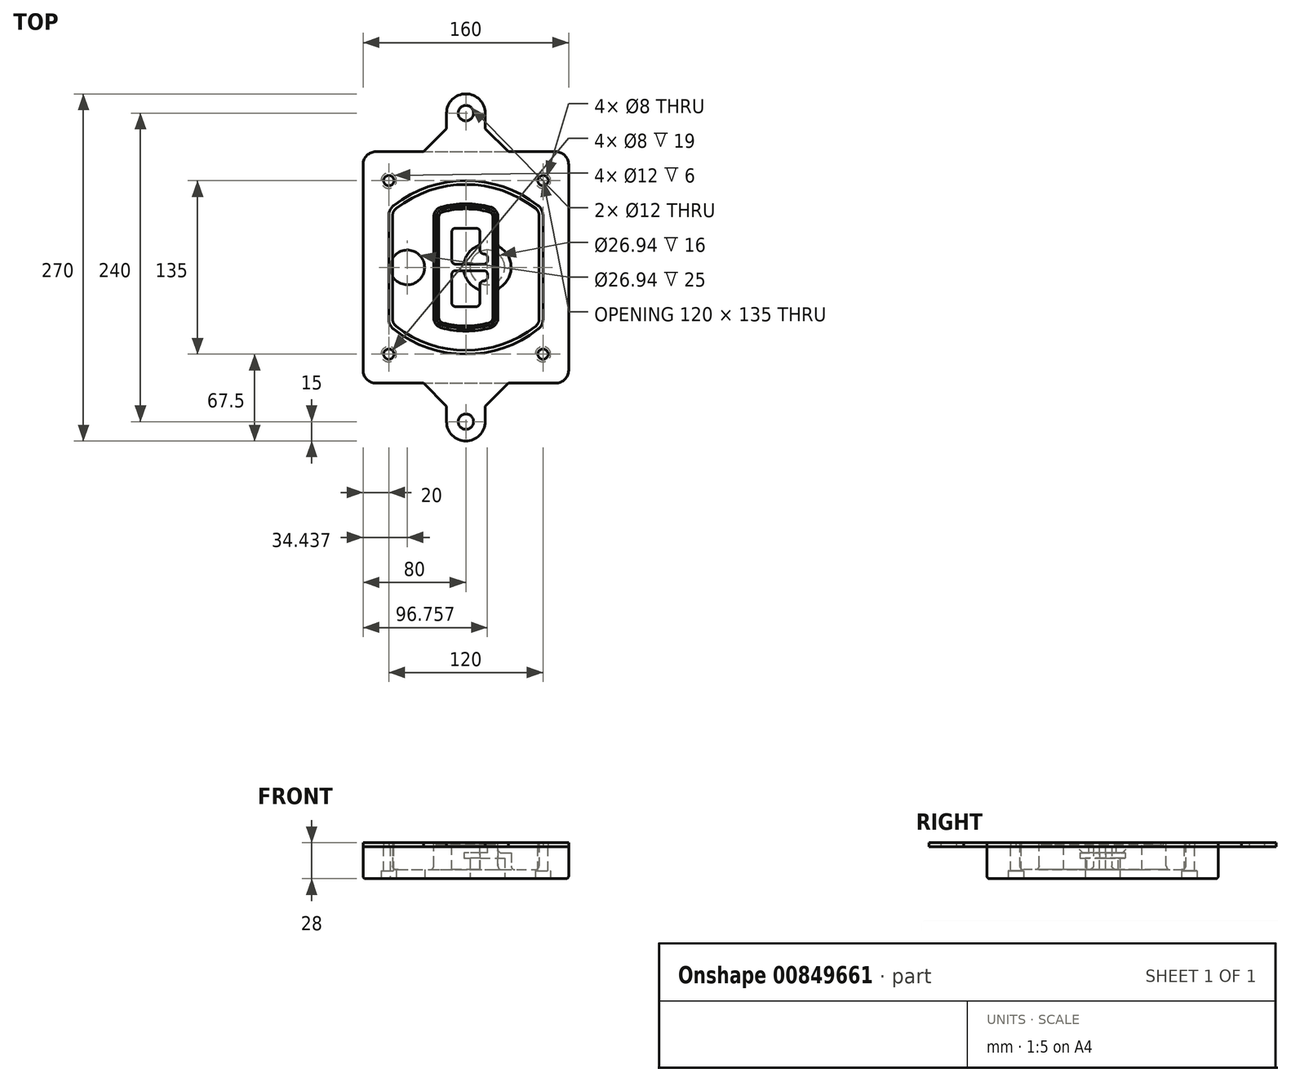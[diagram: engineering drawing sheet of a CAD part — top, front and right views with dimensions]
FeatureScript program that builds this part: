
annotation { "Feature Type Name" : "Feature", "Feature Type Description" : "" }
export const myFeature = defineFeature(function(context is Context, id is Id, definition is map)
    precondition{}
    {
        {
            var Q0;
            Q0=qCreatedBy(makeId("Top.planeOp"),FACE);
            var sketch = newSketch(context, id + "F0", { "sketchPlane" : qUnion([Q0])});
            skPoint(sketch, "E0.rect.middle", {"position": v(0, 0) * mm});
            skLineSegment(sketch, "E1.bottom", {"start": v(-70, -90) * mm, "end": v(70, -90) * mm});
            skLineSegment(sketch, "E1.top", {"start": v(-70, 90) * mm, "end": v(70, 90) * mm});
            skLineSegment(sketch, "E1.left", {"start": v(-80, -80) * mm, "end": v(-80, 80) * mm});
            skLineSegment(sketch, "E1.right", {"start": v(80, -80) * mm, "end": v(80, 80) * mm});
            skLineSegment(sketch, "E2", {"start": v(-80, 90) * mm, "end": v(80, -90) * mm, "construction": true});
            skLineSegment(sketch, "E3", {"start": v(80, 90) * mm, "end": v(-80, -90) * mm, "construction": true});
            skCircle(sketch, "E4", {"center": v(-60, 67.5) * mm, "radius": 4 * mm});
            skCircle(sketch, "E5", {"center": v(60, 67.5) * mm, "radius": 4 * mm});
            skCircle(sketch, "E6", {"center": v(60, -67.5) * mm, "radius": 4 * mm});
            skCircle(sketch, "E7", {"center": v(-60, -67.5) * mm, "radius": 4 * mm});
            skLineSegment(sketch, "E8", {"start": v(-60, 67.5) * mm, "end": v(60, 67.5) * mm, "construction": true});
            skLineSegment(sketch, "E9", {"start": v(60, 67.5) * mm, "end": v(60, -67.5) * mm, "construction": true});
            skLineSegment(sketch, "E10", {"start": v(60, -67.5) * mm, "end": v(-60, -67.5) * mm, "construction": true});
            skLineSegment(sketch, "E11", {"start": v(-60, -67.5) * mm, "end": v(-60, 67.5) * mm, "construction": true});
            skLineSegment(sketch, "E12", {"start": v(-60, 40.3) * mm, "end": v(-60, -40.3) * mm});
            skLineSegment(sketch, "E13", {"start": v(60, 40.3) * mm, "end": v(60, -40.3) * mm});
            skArc(sketch, "E14", {"start": v(56.15, 48.18) * mm, "mid": v(0, 67.5) * mm, "end": v(-56.15, 48.18) * mm});
            skArc(sketch, "E15", {"start": v(-56.15, -48.18) * mm, "mid": v(0, -67.5) * mm, "end": v(56.15, -48.18) * mm});
            skLineSegment(sketch, "E16", {"start": v(-60, 0) * mm, "end": v(60, 0) * mm, "construction": true});
            skPoint(sketch, "E17.visualSharp", {"position": v(-60, -45) * mm});
            skArc(sketch, "E17.filletArc", {"start": v(-60, -40.3) * mm, "mid": v(-58.99, -44.68) * mm, "end": v(-56.15, -48.18) * mm});
            skPoint(sketch, "E18.visualSharp", {"position": v(-60, 45) * mm});
            skArc(sketch, "E18.filletArc", {"start": v(-56.15, 48.18) * mm, "mid": v(-58.99, 44.68) * mm, "end": v(-60, 40.3) * mm});
            skPoint(sketch, "E19.visualSharp", {"position": v(60, 45) * mm});
            skArc(sketch, "E19.filletArc", {"start": v(60, 40.3) * mm, "mid": v(58.99, 44.68) * mm, "end": v(56.15, 48.18) * mm});
            skPoint(sketch, "E20.visualSharp", {"position": v(60, -45) * mm});
            skArc(sketch, "E20.filletArc", {"start": v(56.15, -48.18) * mm, "mid": v(58.99, -44.68) * mm, "end": v(60, -40.3) * mm});
            skPoint(sketch, "E21.visualSharp", {"position": v(-80, 90) * mm});
            skArc(sketch, "E21.filletArc", {"start": v(-70, 90) * mm, "mid": v(-77.07, 87.07) * mm, "end": v(-80, 80) * mm});
            skPoint(sketch, "E22.visualSharp", {"position": v(80, 90) * mm});
            skArc(sketch, "E22.filletArc", {"start": v(80, 80) * mm, "mid": v(77.07, 87.07) * mm, "end": v(70, 90) * mm});
            skPoint(sketch, "E23.visualSharp", {"position": v(80, -90) * mm});
            skArc(sketch, "E23.filletArc", {"start": v(70, -90) * mm, "mid": v(77.07, -87.07) * mm, "end": v(80, -80) * mm});
            skPoint(sketch, "E24.visualSharp", {"position": v(-80, -90) * mm});
            skArc(sketch, "E24.filletArc", {"start": v(-80, -80) * mm, "mid": v(-77.07, -87.07) * mm, "end": v(-70, -90) * mm});
            skArc(sketch, "E25.0", {"start": v(57, 40.3) * mm, "mid": v(56.3, 43.36) * mm, "end": v(54.3, 45.81) * mm});
            skLineSegment(sketch, "E25.1", {"start": v(57, 40.3) * mm, "end": v(57, -40.3) * mm});
            skArc(sketch, "E25.2", {"start": v(54.3, -45.81) * mm, "mid": v(56.3, -43.36) * mm, "end": v(57, -40.3) * mm});
            skArc(sketch, "E25.3", {"start": v(-54.3, -45.81) * mm, "mid": v(0, -64.5) * mm, "end": v(54.3, -45.81) * mm});
            skArc(sketch, "E25.4", {"start": v(-57, -40.3) * mm, "mid": v(-56.3, -43.36) * mm, "end": v(-54.3, -45.81) * mm});
            skArc(sketch, "E25.5", {"start": v(54.3, 45.81) * mm, "mid": v(0, 64.5) * mm, "end": v(-54.3, 45.81) * mm});
            skLineSegment(sketch, "E25.6", {"start": v(-57, 40.3) * mm, "end": v(-57, -40.3) * mm});
            skArc(sketch, "E25.7", {"start": v(-54.3, 45.81) * mm, "mid": v(-56.3, 43.36) * mm, "end": v(-57, 40.3) * mm});
            skArc(sketch, "E26.0", {"start": v(-58.62, 51.33) * mm, "mid": v(-62.58, 46.43) * mm, "end": v(-64, 40.3) * mm});
            skArc(sketch, "E26.1", {"start": v(58.62, 51.33) * mm, "mid": v(0, 71.5) * mm, "end": v(-58.62, 51.33) * mm});
            skArc(sketch, "E26.2", {"start": v(64, 40.3) * mm, "mid": v(62.58, 46.43) * mm, "end": v(58.62, 51.33) * mm});
            skLineSegment(sketch, "E26.3", {"start": v(64, 40.3) * mm, "end": v(64, -40.3) * mm});
            skArc(sketch, "E26.4", {"start": v(58.62, -51.33) * mm, "mid": v(62.58, -46.43) * mm, "end": v(64, -40.3) * mm});
            skLineSegment(sketch, "E26.5", {"start": v(-64, 40.3) * mm, "end": v(-64, -40.3) * mm});
            skArc(sketch, "E26.6", {"start": v(-58.62, -51.33) * mm, "mid": v(0, -71.5) * mm, "end": v(58.62, -51.33) * mm});
            skArc(sketch, "E26.7", {"start": v(-64, -40.3) * mm, "mid": v(-62.58, -46.43) * mm, "end": v(-58.62, -51.33) * mm});
            skSolve(sketch);
        }
        {
            var Q0;
            Q0=makeQuery(id+"F0.imprint","IMPRINT",FACE,{"disambiguationData":[TD([[makeQuery(id+"F0.imprint","IMPRINT",EDGE,{"derivedFrom":sQuery(id+"F0.wireOp",EDGE,"E1.bottom")}),1.0]])]});
            var Q1;
            Q1=makeQuery(id+"F0.imprint","IMPRINT",FACE,{"disambiguationData":[TD([[makeQuery(id+"F0.imprint","IMPRINT",EDGE,{"derivedFrom":sQuery(id+"F0.wireOp",EDGE,"E12")}),1.0]])]});
            var Q2;
            Q2=makeQuery(id+"F0.imprint","IMPRINT",FACE,{"disambiguationData":[TD([[makeQuery(id+"F0.imprint","IMPRINT",EDGE,{"derivedFrom":sQuery(id+"F0.wireOp",EDGE,"E25.0")}),1.0]])]});
            var Q3;
            Q3=makeQuery(id+"F0.imprint","IMPRINT",FACE,{"disambiguationData":[TD([[makeQuery(id+"F0.imprint","IMPRINT",EDGE,{"derivedFrom":sQuery(id+"F0.wireOp",EDGE,"E12")}),-1.0]])]});
            extrude(context, id + "F1", {"entities" : qUnion([Q0, Q1, Q2, Q3]), "oppositeDirection" : true, "depth" : 25 * mm});
        }
        {
            var Q0;
            Q0=makeQuery(id+"F0.imprint","IMPRINT",FACE,{"disambiguationData":[TD([[makeQuery(id+"F0.imprint","IMPRINT",EDGE,{"derivedFrom":sQuery(id+"F0.wireOp",EDGE,"E12")}),1.0]])]});
            extrude(context, id + "F2", {"entities" : qUnion([Q0]), "operationType" : NewBodyOperationType.ADD, "depth" : 3 * mm});
        }
        {
            var Q0;
            Q0=makeQuery(id+"F0.imprint","IMPRINT",FACE,{"disambiguationData":[TD([[makeQuery(id+"F0.imprint","IMPRINT",EDGE,{"derivedFrom":sQuery(id+"F0.wireOp",EDGE,"E25.0")}),1.0]])]});
            extrude(context, id + "F3", {"entities" : qUnion([Q0]), "operationType" : NewBodyOperationType.REMOVE, "oppositeDirection" : true, "depth" : 18 * mm});
        }
        {
            var Q0;
            Q0=makeQuery(id+"F2.opExtrude","CAP_FACE",FACE,{"disambiguationData":[OSD([sQuery(id+"F0.wireOp",EDGE,"E12"),sQuery(id+"F0.wireOp",EDGE,"E13"),sQuery(id+"F0.wireOp",EDGE,"E14"),sQuery(id+"F0.wireOp",EDGE,"E15"),sQuery(id+"F0.wireOp",EDGE,"E17.filletArc"),sQuery(id+"F0.wireOp",EDGE,"E18.filletArc"),sQuery(id+"F0.wireOp",EDGE,"E19.filletArc"),sQuery(id+"F0.wireOp",EDGE,"E20.filletArc"),sQuery(id+"F0.wireOp",EDGE,"E25.0"),sQuery(id+"F0.wireOp",EDGE,"E25.1"),sQuery(id+"F0.wireOp",EDGE,"E25.2"),sQuery(id+"F0.wireOp",EDGE,"E25.3"),sQuery(id+"F0.wireOp",EDGE,"E25.4"),sQuery(id+"F0.wireOp",EDGE,"E25.5"),sQuery(id+"F0.wireOp",EDGE,"E25.6"),sQuery(id+"F0.wireOp",EDGE,"E25.7")])],"isStart":false});
            var sketch = newSketch(context, id + "F4", { "sketchPlane" : qUnion([Q0])});
            skArc(sketch, "E27.0", {"start": v(-19.08, -46.97) * mm, "mid": v(0, -49.5) * mm, "end": v(19.08, -46.97) * mm});
            skArc(sketch, "E28.0", {"start": v(19.08, 46.97) * mm, "mid": v(0, 49.5) * mm, "end": v(-19.08, 46.97) * mm});
            skLineSegment(sketch, "E29", {"start": v(-25, 39.25) * mm, "end": v(-25, -39.25) * mm});
            skLineSegment(sketch, "E30", {"start": v(25, 39.25) * mm, "end": v(25, -39.25) * mm});
            skLineSegment(sketch, "E31", {"start": v(-25, 45.1) * mm, "end": v(25, 45.1) * mm, "construction": true});
            skLineSegment(sketch, "E32", {"start": v(-25, -45.1) * mm, "end": v(25, -45.1) * mm, "construction": true});
            skPoint(sketch, "E33.visualSharp", {"position": v(-25, 45.1) * mm});
            skArc(sketch, "E33.filletArc", {"start": v(-19.08, 46.97) * mm, "mid": v(-23.35, 44.11) * mm, "end": v(-25, 39.25) * mm});
            skPoint(sketch, "E34.visualSharp", {"position": v(25, 45.1) * mm});
            skArc(sketch, "E34.filletArc", {"start": v(25, 39.25) * mm, "mid": v(23.35, 44.11) * mm, "end": v(19.08, 46.97) * mm});
            skPoint(sketch, "E35.visualSharp", {"position": v(25, -45.1) * mm});
            skArc(sketch, "E35.filletArc", {"start": v(19.08, -46.97) * mm, "mid": v(23.35, -44.11) * mm, "end": v(25, -39.25) * mm});
            skPoint(sketch, "E36.visualSharp", {"position": v(-25, -45.1) * mm});
            skArc(sketch, "E36.filletArc", {"start": v(-25, -39.25) * mm, "mid": v(-23.35, -44.11) * mm, "end": v(-19.08, -46.97) * mm});
            skArc(sketch, "E37.0", {"start": v(54.3, 45.81) * mm, "mid": v(0, 64.5) * mm, "end": v(-54.3, 45.81) * mm});
            skArc(sketch, "E37.1", {"start": v(-54.3, 45.81) * mm, "mid": v(-56.3, 43.36) * mm, "end": v(-57, 40.3) * mm});
            skLineSegment(sketch, "E37.2", {"start": v(-57, 40.3) * mm, "end": v(-57, -40.3) * mm});
            skArc(sketch, "E37.3", {"start": v(-57, -40.3) * mm, "mid": v(-56.3, -43.36) * mm, "end": v(-54.3, -45.81) * mm});
            skArc(sketch, "E37.4", {"start": v(-54.3, -45.81) * mm, "mid": v(0, -64.5) * mm, "end": v(54.3, -45.81) * mm});
            skArc(sketch, "E37.5", {"start": v(54.3, -45.81) * mm, "mid": v(56.3, -43.36) * mm, "end": v(57, -40.3) * mm});
            skLineSegment(sketch, "E37.6", {"start": v(57, 40.3) * mm, "end": v(57, -40.3) * mm});
            skArc(sketch, "E37.7", {"start": v(57, 40.3) * mm, "mid": v(56.3, 43.36) * mm, "end": v(54.3, 45.81) * mm});
            skLineSegment(sketch, "E38.0", {"start": v(23, 39.25) * mm, "end": v(23, -39.25) * mm});
            skArc(sketch, "E38.1", {"start": v(18.56, -45.04) * mm, "mid": v(21.76, -42.9) * mm, "end": v(23, -39.25) * mm});
            skArc(sketch, "E38.2", {"start": v(-18.56, -45.04) * mm, "mid": v(0, -47.5) * mm, "end": v(18.56, -45.04) * mm});
            skArc(sketch, "E38.3", {"start": v(-23, -39.25) * mm, "mid": v(-21.76, -42.9) * mm, "end": v(-18.56, -45.04) * mm});
            skLineSegment(sketch, "E38.4", {"start": v(-23, 39.25) * mm, "end": v(-23, -39.25) * mm});
            skArc(sketch, "E38.5", {"start": v(23, 39.25) * mm, "mid": v(21.76, 42.9) * mm, "end": v(18.56, 45.04) * mm});
            skArc(sketch, "E38.6", {"start": v(-18.56, 45.04) * mm, "mid": v(-21.76, 42.9) * mm, "end": v(-23, 39.25) * mm});
            skArc(sketch, "E38.7", {"start": v(18.56, 45.04) * mm, "mid": v(0, 47.5) * mm, "end": v(-18.56, 45.04) * mm});
            skArc(sketch, "E39.0", {"start": v(21, 39.25) * mm, "mid": v(20.18, 41.68) * mm, "end": v(18.04, 43.1) * mm});
            skLineSegment(sketch, "E39.1", {"start": v(21, 39.25) * mm, "end": v(21, -39.25) * mm});
            skArc(sketch, "E39.2", {"start": v(18.04, -43.1) * mm, "mid": v(20.18, -41.68) * mm, "end": v(21, -39.25) * mm});
            skArc(sketch, "E39.3", {"start": v(-18.04, -43.1) * mm, "mid": v(0, -45.5) * mm, "end": v(18.04, -43.1) * mm});
            skArc(sketch, "E39.4", {"start": v(-21, -39.25) * mm, "mid": v(-20.18, -41.68) * mm, "end": v(-18.04, -43.1) * mm});
            skArc(sketch, "E39.5", {"start": v(18.04, 43.1) * mm, "mid": v(0, 45.5) * mm, "end": v(-18.04, 43.1) * mm});
            skLineSegment(sketch, "E39.6", {"start": v(-21, 39.25) * mm, "end": v(-21, -39.25) * mm});
            skArc(sketch, "E39.7", {"start": v(-18.04, 43.1) * mm, "mid": v(-20.18, 41.68) * mm, "end": v(-21, 39.25) * mm});
            skLineSegment(sketch, "E40", {"start": v(-25, 0) * mm, "end": v(25, 0) * mm, "construction": true});
            skLineSegment(sketch, "E41", {"start": v(-11, 5.5) * mm, "end": v(-11, 27.5) * mm});
            skLineSegment(sketch, "E42", {"start": v(-8, 30.5) * mm, "end": v(8, 30.5) * mm});
            skLineSegment(sketch, "E43", {"start": v(11, 27.5) * mm, "end": v(11, 13.5) * mm});
            skLineSegment(sketch, "E44", {"start": v(14, 10.5) * mm, "end": v(14, 10.5) * mm});
            skLineSegment(sketch, "E45", {"start": v(17, 7.5) * mm, "end": v(17, 5.5) * mm});
            skLineSegment(sketch, "E46", {"start": v(14, 2.5) * mm, "end": v(-8, 2.5) * mm});
            skPoint(sketch, "E47.visualSharp", {"position": v(-11, 30.5) * mm});
            skArc(sketch, "E47.filletArc", {"start": v(-8, 30.5) * mm, "mid": v(-10.12, 29.62) * mm, "end": v(-11, 27.5) * mm});
            skPoint(sketch, "E48.visualSharp", {"position": v(11, 30.5) * mm});
            skArc(sketch, "E48.filletArc", {"start": v(11, 27.5) * mm, "mid": v(10.12, 29.62) * mm, "end": v(8, 30.5) * mm});
            skPoint(sketch, "E49.visualSharp", {"position": v(11, 10.5) * mm});
            skArc(sketch, "E49.filletArc", {"start": v(11, 13.5) * mm, "mid": v(11.88, 11.38) * mm, "end": v(14, 10.5) * mm});
            skPoint(sketch, "E50.visualSharp", {"position": v(17, 10.5) * mm});
            skArc(sketch, "E50.filletArc", {"start": v(17, 7.5) * mm, "mid": v(16.12, 9.62) * mm, "end": v(14, 10.5) * mm});
            skPoint(sketch, "E51.visualSharp", {"position": v(17, 2.5) * mm});
            skArc(sketch, "E51.filletArc", {"start": v(14, 2.5) * mm, "mid": v(16.12, 3.38) * mm, "end": v(17, 5.5) * mm});
            skPoint(sketch, "E52.visualSharp", {"position": v(-11, 2.5) * mm});
            skArc(sketch, "E52.filletArc", {"start": v(-11, 5.5) * mm, "mid": v(-10.12, 3.38) * mm, "end": v(-8, 2.5) * mm});
            skLineSegment(sketch, "E53.0.MirrorCS", {"start": v(14, -2.5) * mm, "end": v(-8, -2.5) * mm});
            skArc(sketch, "E54.0.MirrorCS", {"start": v(-11, -5.5) * mm, "mid": v(-10.12, -3.38) * mm, "end": v(-8, -2.5) * mm});
            skLineSegment(sketch, "E55.0.MirrorCS", {"start": v(-11, -5.5) * mm, "end": v(-11, -27.5) * mm});
            skArc(sketch, "E56.0.MirrorCS", {"start": v(-8, -30.5) * mm, "mid": v(-10.12, -29.62) * mm, "end": v(-11, -27.5) * mm});
            skLineSegment(sketch, "E57.0.MirrorCS", {"start": v(-8, -30.5) * mm, "end": v(8, -30.5) * mm});
            skArc(sketch, "E58.0.MirrorCS", {"start": v(11, -27.5) * mm, "mid": v(10.12, -29.62) * mm, "end": v(8, -30.5) * mm});
            skLineSegment(sketch, "E59.0.MirrorCS", {"start": v(11, -27.5) * mm, "end": v(11, -13.5) * mm});
            skArc(sketch, "E60.0.MirrorCS", {"start": v(11, -13.5) * mm, "mid": v(11.88, -11.38) * mm, "end": v(14, -10.5) * mm});
            skArc(sketch, "E61.0.MirrorCS", {"start": v(17, -7.5) * mm, "mid": v(16.12, -9.62) * mm, "end": v(14, -10.5) * mm});
            skLineSegment(sketch, "E62.0.MirrorCS", {"start": v(17, -7.5) * mm, "end": v(17, -5.5) * mm});
            skArc(sketch, "E63.0.MirrorCS", {"start": v(14, -2.5) * mm, "mid": v(16.12, -3.38) * mm, "end": v(17, -5.5) * mm});
            skSolve(sketch);
        }
        {
            var Q0;
            Q0=makeQuery(id+"F4.imprint","IMPRINT",FACE,{"disambiguationData":[TD([[makeQuery(id+"F4.imprint","IMPRINT",EDGE,{"derivedFrom":sQuery(id+"F4.wireOp",EDGE,"E27.0")}),1.0]])]});
            var Q1;
            Q1=makeQuery(id+"F4.imprint","IMPRINT",FACE,{"disambiguationData":[TD([[makeQuery(id+"F4.imprint","IMPRINT",EDGE,{"derivedFrom":sQuery(id+"F4.wireOp",EDGE,"E38.0")}),-1.0]])]});
            var Q2;
            Q2=makeQuery(id+"F4.imprint","IMPRINT",FACE,{"disambiguationData":[TD([[makeQuery(id+"F4.imprint","IMPRINT",EDGE,{"derivedFrom":sQuery(id+"F4.wireOp",EDGE,"E39.0")}),1.0]])]});
            extrude(context, id + "F5", {"entities" : qUnion([Q0, Q1, Q2]), "operationType" : NewBodyOperationType.ADD, "endBound" : BoundingType.UP_TO_NEXT, "oppositeDirection" : true, "depth" : 25 * mm});
        }
        {
            var Q0;
            Q0=makeQuery(id+"F4.imprint","IMPRINT",FACE,{"disambiguationData":[TD([[makeQuery(id+"F4.imprint","IMPRINT",EDGE,{"derivedFrom":sQuery(id+"F4.wireOp",EDGE,"E38.0")}),-1.0]])]});
            extrude(context, id + "F6", {"entities" : qUnion([Q0]), "operationType" : NewBodyOperationType.REMOVE, "oppositeDirection" : true, "depth" : 2 * mm});
        }
        {
            var Q0;
            Q0=makeQuery(id+"F1.opExtrude","CAP_FACE",FACE,{"disambiguationData":[OSD([sQuery(id+"F0.wireOp",EDGE,"E1.bottom"),sQuery(id+"F0.wireOp",EDGE,"E1.top"),sQuery(id+"F0.wireOp",EDGE,"E1.left"),sQuery(id+"F0.wireOp",EDGE,"E1.right"),sQuery(id+"F0.wireOp",EDGE,"E4"),sQuery(id+"F0.wireOp",EDGE,"E5"),sQuery(id+"F0.wireOp",EDGE,"E6"),sQuery(id+"F0.wireOp",EDGE,"E7"),sQuery(id+"F0.wireOp",EDGE,"E21.filletArc"),sQuery(id+"F0.wireOp",EDGE,"E22.filletArc"),sQuery(id+"F0.wireOp",EDGE,"E23.filletArc"),sQuery(id+"F0.wireOp",EDGE,"E24.filletArc")])],"isStart":false});
            var sketch = newSketch(context, id + "F7", { "sketchPlane" : qUnion([Q0])});
            skCircle(sketch, "E64", {"center": v(16.76, 0) * mm, "radius": 13.47 * mm});
            skCircle(sketch, "E65", {"center": v(-45.56, 0) * mm, "radius": 13.47 * mm});
            skLineSegment(sketch, "E66", {"start": v(80, 0) * mm, "end": v(-80, 0) * mm});
            skCircle(sketch, "E67", {"center": v(16.76, 0) * mm, "radius": 18.47 * mm});
            skCircle(sketch, "E68", {"center": v(60, -67.5) * mm, "radius": 6 * mm});
            skCircle(sketch, "E69", {"center": v(-60, -67.5) * mm, "radius": 6 * mm});
            skCircle(sketch, "E70", {"center": v(-60, 67.5) * mm, "radius": 6 * mm});
            skCircle(sketch, "E71", {"center": v(60, 67.5) * mm, "radius": 6 * mm});
            skSolve(sketch);
        }
        {
            var Q0;
            {var subQ1=sQuery(id+"F7.wireOp",EDGE,"E66");var subQ4=sQuery(id+"F7.wireOp",EDGE,"E64");var subQ6=makeQuery(id+"F7.imprint","INTERSECT",VERTEX,{"disambiguationData":[OD(0.0)],"derivedFrom":[subQ4,subQ1]});Q0=makeQuery(id+"F7.imprint","IMPRINT",FACE,{"disambiguationData":[TD([[makeQuery(id+"F7.imprint","IMPRINT",EDGE,{"disambiguationData":[TD([[subQ6,-1.0]])],"derivedFrom":subQ4}),-1.0]])]});}
            var Q1;
            {var subQ0=sQuery(id+"F7.wireOp",EDGE,"E66");var subQ1=sQuery(id+"F7.wireOp",EDGE,"E64");var subQ3=makeQuery(id+"F7.imprint","INTERSECT",VERTEX,{"disambiguationData":[OD(0.0)],"derivedFrom":[subQ1,subQ0]});Q1=makeQuery(id+"F7.imprint","IMPRINT",FACE,{"disambiguationData":[TD([[makeQuery(id+"F7.imprint","IMPRINT",EDGE,{"disambiguationData":[TD([[subQ3,-1.0]])],"derivedFrom":subQ1}),1.0]])]});}
            var Q2;
            {var subQ0=sQuery(id+"F7.wireOp",EDGE,"E66");var subQ1=sQuery(id+"F7.wireOp",EDGE,"E64");var subQ3=makeQuery(id+"F7.imprint","INTERSECT",VERTEX,{"disambiguationData":[OD(0.0)],"derivedFrom":[subQ1,subQ0]});Q2=makeQuery(id+"F7.imprint","IMPRINT",FACE,{"disambiguationData":[TD([[makeQuery(id+"F7.imprint","IMPRINT",EDGE,{"disambiguationData":[TD([[subQ3,1.0]])],"derivedFrom":subQ1}),1.0]])]});}
            var Q3;
            {var subQ1=sQuery(id+"F7.wireOp",EDGE,"E66");var subQ4=sQuery(id+"F7.wireOp",EDGE,"E64");var subQ6=makeQuery(id+"F7.imprint","INTERSECT",VERTEX,{"disambiguationData":[OD(0.0)],"derivedFrom":[subQ4,subQ1]});Q3=makeQuery(id+"F7.imprint","IMPRINT",FACE,{"disambiguationData":[TD([[makeQuery(id+"F7.imprint","IMPRINT",EDGE,{"disambiguationData":[TD([[subQ6,1.0]])],"derivedFrom":subQ4}),-1.0]])]});}
            extrude(context, id + "F8", {"entities" : qUnion([Q0, Q1, Q2, Q3]), "operationType" : NewBodyOperationType.ADD, "oppositeDirection" : true, "depth" : 20 * mm});
        }
        {
            var Q0;
            {var subQ0=sQuery(id+"F7.wireOp",EDGE,"E66");var subQ1=sQuery(id+"F7.wireOp",EDGE,"E64");var subQ3=makeQuery(id+"F7.imprint","INTERSECT",VERTEX,{"disambiguationData":[OD(0.0)],"derivedFrom":[subQ1,subQ0]});Q0=makeQuery(id+"F7.imprint","IMPRINT",FACE,{"disambiguationData":[TD([[makeQuery(id+"F7.imprint","IMPRINT",EDGE,{"disambiguationData":[TD([[subQ3,-1.0]])],"derivedFrom":subQ1}),1.0]])]});}
            var Q1;
            {var subQ0=sQuery(id+"F7.wireOp",EDGE,"E66");var subQ1=sQuery(id+"F7.wireOp",EDGE,"E64");var subQ3=makeQuery(id+"F7.imprint","INTERSECT",VERTEX,{"disambiguationData":[OD(0.0)],"derivedFrom":[subQ1,subQ0]});Q1=makeQuery(id+"F7.imprint","IMPRINT",FACE,{"disambiguationData":[TD([[makeQuery(id+"F7.imprint","IMPRINT",EDGE,{"disambiguationData":[TD([[subQ3,1.0]])],"derivedFrom":subQ1}),1.0]])]});}
            extrude(context, id + "F9", {"entities" : qUnion([Q0, Q1]), "operationType" : NewBodyOperationType.REMOVE, "oppositeDirection" : true, "depth" : 16 * mm});
        }
        {
            var Q0;
            {var subQ0=sQuery(id+"F7.wireOp",EDGE,"E66");var subQ1=sQuery(id+"F7.wireOp",EDGE,"E65");var subQ3=makeQuery(id+"F7.imprint","INTERSECT",VERTEX,{"disambiguationData":[OD(0.0)],"derivedFrom":[subQ1,subQ0]});Q0=makeQuery(id+"F7.imprint","IMPRINT",FACE,{"disambiguationData":[TD([[makeQuery(id+"F7.imprint","IMPRINT",EDGE,{"disambiguationData":[TD([[subQ3,-1.0]])],"derivedFrom":subQ1}),1.0]])]});}
            var Q1;
            {var subQ0=sQuery(id+"F7.wireOp",EDGE,"E66");var subQ1=sQuery(id+"F7.wireOp",EDGE,"E65");var subQ3=makeQuery(id+"F7.imprint","INTERSECT",VERTEX,{"disambiguationData":[OD(0.0)],"derivedFrom":[subQ1,subQ0]});Q1=makeQuery(id+"F7.imprint","IMPRINT",FACE,{"disambiguationData":[TD([[makeQuery(id+"F7.imprint","IMPRINT",EDGE,{"disambiguationData":[TD([[subQ3,1.0]])],"derivedFrom":subQ1}),1.0]])]});}
            extrude(context, id + "F10", {"entities" : qUnion([Q0, Q1]), "operationType" : NewBodyOperationType.REMOVE, "oppositeDirection" : true, "depth" : 25 * mm});
        }
        {
            var Q0;
            Q0=makeQuery(id+"F7.imprint","IMPRINT",FACE,{"disambiguationData":[TD([[makeQuery(id+"F7.imprint","IMPRINT",EDGE,{"derivedFrom":sQuery(id+"F7.wireOp",EDGE,"E68")}),1.0]])]});
            var Q1;
            Q1=makeQuery(id+"F7.imprint","IMPRINT",FACE,{"disambiguationData":[TD([[makeQuery(id+"F7.imprint","IMPRINT",EDGE,{"derivedFrom":makeQuery(id+"F1.opExtrude","CAP_EDGE",EDGE,{"disambiguationData":[OSD([sQuery(id+"F0.wireOp",EDGE,"E5")])],"isStart":false})}),-1.0]])]});
            var Q2;
            Q2=makeQuery(id+"F7.imprint","IMPRINT",FACE,{"disambiguationData":[TD([[makeQuery(id+"F7.imprint","IMPRINT",EDGE,{"derivedFrom":sQuery(id+"F7.wireOp",EDGE,"E69")}),1.0]])]});
            var Q3;
            Q3=makeQuery(id+"F7.imprint","IMPRINT",FACE,{"disambiguationData":[TD([[makeQuery(id+"F7.imprint","IMPRINT",EDGE,{"derivedFrom":makeQuery(id+"F1.opExtrude","CAP_EDGE",EDGE,{"disambiguationData":[OSD([sQuery(id+"F0.wireOp",EDGE,"E4")])],"isStart":false})}),-1.0]])]});
            var Q4;
            Q4=makeQuery(id+"F7.imprint","IMPRINT",FACE,{"disambiguationData":[TD([[makeQuery(id+"F7.imprint","IMPRINT",EDGE,{"derivedFrom":sQuery(id+"F7.wireOp",EDGE,"E70")}),1.0]])]});
            var Q5;
            Q5=makeQuery(id+"F7.imprint","IMPRINT",FACE,{"disambiguationData":[TD([[makeQuery(id+"F7.imprint","IMPRINT",EDGE,{"derivedFrom":makeQuery(id+"F1.opExtrude","CAP_EDGE",EDGE,{"disambiguationData":[OSD([sQuery(id+"F0.wireOp",EDGE,"E7")])],"isStart":false})}),-1.0]])]});
            var Q6;
            Q6=makeQuery(id+"F7.imprint","IMPRINT",FACE,{"disambiguationData":[TD([[makeQuery(id+"F7.imprint","IMPRINT",EDGE,{"derivedFrom":sQuery(id+"F7.wireOp",EDGE,"E71")}),1.0]])]});
            var Q7;
            Q7=makeQuery(id+"F7.imprint","IMPRINT",FACE,{"disambiguationData":[TD([[makeQuery(id+"F7.imprint","IMPRINT",EDGE,{"derivedFrom":makeQuery(id+"F1.opExtrude","CAP_EDGE",EDGE,{"disambiguationData":[OSD([sQuery(id+"F0.wireOp",EDGE,"E6")])],"isStart":false})}),-1.0]])]});
            extrude(context, id + "F11", {"entities" : qUnion([Q0, Q1, Q2, Q3, Q4, Q5, Q6, Q7]), "operationType" : NewBodyOperationType.REMOVE, "oppositeDirection" : true, "depth" : 6 * mm});
        }
        {
            var Q0;
            Q0=makeQuery(id+"F9.boolean.opBoolean","COPY",FACE,{"derivedFrom":makeQuery(id+"F9.opExtrude","CAP_FACE",FACE,{"disambiguationData":[OSD([sQuery(id+"F7.wireOp",EDGE,"E64")])],"isStart":false})});
            var sketch = newSketch(context, id + "F12", { "sketchPlane" : qUnion([Q0])});
            skArc(sketch, "E72.0", {"start": v(11, 17.55) * mm, "mid": v(2.57, 11.82) * mm, "end": v(-1.54, 2.5) * mm});
            skArc(sketch, "E72.1", {"start": v(-1.54, -2.5) * mm, "mid": v(2.57, -11.82) * mm, "end": v(11, -17.55) * mm});
            skLineSegment(sketch, "E73", {"start": v(-1.54, -2.5) * mm, "end": v(14, -2.5) * mm});
            skLineSegment(sketch, "E74.0", {"start": v(14, 2.5) * mm, "end": v(-1.54, 2.5) * mm});
            skArc(sketch, "E74.1", {"start": v(14, 2.5) * mm, "mid": v(16.12, 3.38) * mm, "end": v(17, 5.5) * mm});
            skLineSegment(sketch, "E74.2", {"start": v(17, 7.5) * mm, "end": v(17, 5.5) * mm});
            skArc(sketch, "E74.3", {"start": v(17, 7.5) * mm, "mid": v(16.12, 9.62) * mm, "end": v(14, 10.5) * mm});
            skArc(sketch, "E74.4", {"start": v(11, 13.5) * mm, "mid": v(11.88, 11.38) * mm, "end": v(14, 10.5) * mm});
            skLineSegment(sketch, "E74.5", {"start": v(11, 17.55) * mm, "end": v(11, 13.5) * mm});
            skLineSegment(sketch, "E74.7", {"start": v(14, -2.5) * mm, "end": v(-1.54, -2.5) * mm});
            skArc(sketch, "E74.8", {"start": v(14, -2.5) * mm, "mid": v(16.12, -3.38) * mm, "end": v(17, -5.5) * mm});
            skLineSegment(sketch, "E74.9", {"start": v(17, -7.5) * mm, "end": v(17, -5.5) * mm});
            skArc(sketch, "E74.10", {"start": v(17, -7.5) * mm, "mid": v(16.12, -9.62) * mm, "end": v(14, -10.5) * mm});
            skArc(sketch, "E74.11", {"start": v(11, -13.5) * mm, "mid": v(11.88, -11.38) * mm, "end": v(14, -10.5) * mm});
            skLineSegment(sketch, "E74.12", {"start": v(11, -17.55) * mm, "end": v(11, -13.5) * mm});
            skPoint(sketch, "E75.orphan", {"position": v(11, -27.5) * mm});
            skPoint(sketch, "E76.orphan", {"position": v(-8, -2.5) * mm});
            skPoint(sketch, "E77.orphan", {"position": v(-8, 2.5) * mm});
            skPoint(sketch, "E78.orphan", {"position": v(11, 27.5) * mm});
            skSolve(sketch);
        }
        {
            var Q0;
            {var subQ7=sQuery(id+"F12.wireOp",EDGE,"E72.0");var subQ14=sQuery(id+"F12.wireOp",EDGE,"E72.1");var subQ16=sQuery(id+"F12.wireOp",EDGE,"E74.1");var subQ18=sQuery(id+"F12.wireOp",EDGE,"E74.8");Q0=qUnion([makeQuery(id+"F12.imprint","IMPRINT",FACE,{"disambiguationData":[TD([[makeQuery(id+"F12.imprint","IMPRINT",EDGE,{"derivedFrom":subQ7}),1.0]])]}),makeQuery(id+"F12.imprint","IMPRINT",FACE,{"disambiguationData":[TD([[makeQuery(id+"F12.imprint","IMPRINT",EDGE,{"derivedFrom":subQ14}),1.0]])]}),makeQuery(id+"F12.imprint","IMPRINT",FACE,{"disambiguationData":[TD([[makeQuery(id+"F12.imprint","IMPRINT",EDGE,{"derivedFrom":subQ16}),1.0]])]}),makeQuery(id+"F12.imprint","IMPRINT",FACE,{"disambiguationData":[TD([[makeQuery(id+"F12.imprint","IMPRINT",EDGE,{"derivedFrom":subQ18}),-1.0]])]})]);}
            var Q1;
            Q1=makeQuery(id+"F5.boolean.opBoolean","SPLIT",FACE,{"disambiguationData":[TD([makeQuery(id+"F5.opExtrude","SWEPT_FACE",FACE,{"disambiguationData":[OSD([sQuery(id+"F4.wireOp",EDGE,"E41")])]})])],"derivedFrom":makeQuery(id+"F3.boolean.opBoolean","COPY",FACE,{"derivedFrom":makeQuery(id+"F3.opExtrude","CAP_FACE",FACE,{"disambiguationData":[OSD([sQuery(id+"F0.wireOp",EDGE,"E25.0"),sQuery(id+"F0.wireOp",EDGE,"E25.1"),sQuery(id+"F0.wireOp",EDGE,"E25.2"),sQuery(id+"F0.wireOp",EDGE,"E25.3"),sQuery(id+"F0.wireOp",EDGE,"E25.4"),sQuery(id+"F0.wireOp",EDGE,"E25.5"),sQuery(id+"F0.wireOp",EDGE,"E25.6"),sQuery(id+"F0.wireOp",EDGE,"E25.7")])],"isStart":false})})});
            extrude(context, id + "F13", {"entities" : qUnion([Q0]), "operationType" : NewBodyOperationType.REMOVE, "endBound" : BoundingType.UP_TO_SURFACE, "endBoundEntityFace" : qUnion([Q1]), "depth" : 25 * mm});
        }
        {
            var Q0;
            Q0=makeQuery(id+"F3.boolean.opBoolean","COPY",EDGE,{"derivedFrom":makeQuery(id+"F3.opExtrude","CAP_EDGE",EDGE,{"disambiguationData":[OSD([sQuery(id+"F0.wireOp",EDGE,"E25.6")])],"isStart":false})});
            var Q1;
            Q1=makeQuery(id+"F8.boolean.opBoolean","INTERSECT",EDGE,{"derivedFrom":[makeQuery(id+"F5.opExtrude","SWEPT_FACE",FACE,{"disambiguationData":[OSD([sQuery(id+"F4.wireOp",EDGE,"E30")])]}),makeQuery(id+"F8.opExtrude","CAP_FACE",FACE,{"disambiguationData":[OSD([sQuery(id+"F7.wireOp",EDGE,"E67")])],"isStart":false})]});
            var Q2;
            Q2=makeQuery(id+"F8.boolean.opBoolean","INTERSECT",EDGE,{"disambiguationData":[OD(1.0)],"derivedFrom":[makeQuery(id+"F5.opExtrude","SWEPT_FACE",FACE,{"disambiguationData":[OSD([sQuery(id+"F4.wireOp",EDGE,"E30")])]}),makeQuery(id+"F8.opExtrude","SWEPT_FACE",FACE,{"disambiguationData":[OSD([sQuery(id+"F7.wireOp",EDGE,"E67")])]})]});
            var Q3;
            {var subQ0=sQuery(id+"F4.wireOp",EDGE,"E30");Q3=makeQuery(id+"F8.boolean.opBoolean","SPLIT",EDGE,{"disambiguationData":[TD([makeQuery(id+"F5.opExtrude","SWEPT_FACE",FACE,{"disambiguationData":[OSD([sQuery(id+"F4.wireOp",EDGE,"E35.filletArc")])]})])],"derivedFrom":makeQuery(id+"F5.opExtrude","CAP_EDGE",EDGE,{"disambiguationData":[OSD([subQ0])],"isStart":false})});}
            var Q4;
            {var subQ0=sQuery(id+"F0.wireOp",EDGE,"E25.7");var subQ1=sQuery(id+"F0.wireOp",EDGE,"E25.1");var subQ2=sQuery(id+"F0.wireOp",EDGE,"E25.6");var subQ3=sQuery(id+"F0.wireOp",EDGE,"E25.5");var subQ4=sQuery(id+"F0.wireOp",EDGE,"E25.4");var subQ5=sQuery(id+"F0.wireOp",EDGE,"E25.0");var subQ6=sQuery(id+"F0.wireOp",EDGE,"E25.2");var subQ7=sQuery(id+"F0.wireOp",EDGE,"E25.3");Q4=makeQuery(id+"F8.boolean.opBoolean","INTERSECT",EDGE,{"derivedFrom":[makeQuery(id+"F5.boolean.opBoolean","SPLIT",FACE,{"disambiguationData":[TD([makeQuery(id+"F2.opExtrude","SWEPT_FACE",FACE,{"disambiguationData":[OSD([subQ5])]})])],"derivedFrom":makeQuery(id+"F3.boolean.opBoolean","COPY",FACE,{"derivedFrom":makeQuery(id+"F3.opExtrude","CAP_FACE",FACE,{"disambiguationData":[OSD([subQ5,subQ1,subQ6,subQ7,subQ4,subQ3,subQ2,subQ0])],"isStart":false})})}),makeQuery(id+"F8.opExtrude","SWEPT_FACE",FACE,{"disambiguationData":[OSD([sQuery(id+"F7.wireOp",EDGE,"E67")])]})]});}
            var Q5;
            Q5=makeQuery(id+"F8.boolean.opBoolean","INTERSECT",EDGE,{"disambiguationData":[OD(0.0)],"derivedFrom":[makeQuery(id+"F5.opExtrude","SWEPT_FACE",FACE,{"disambiguationData":[OSD([sQuery(id+"F4.wireOp",EDGE,"E30")])]}),makeQuery(id+"F8.opExtrude","SWEPT_FACE",FACE,{"disambiguationData":[OSD([sQuery(id+"F7.wireOp",EDGE,"E67")])]})]});
            fillet(context, id + "F14", {"entities" : qUnion([Q0, Q1, Q2, Q3, Q4, Q5]), "radius" : 3 * mm, "tangentPropagation" : true, "allowEdgeOverflow" : false});
        }
        {
            var Q0;
            Q0=makeQuery(id+"F1.opExtrude","CAP_EDGE",EDGE,{"disambiguationData":[OSD([sQuery(id+"F0.wireOp",EDGE,"E1.bottom")])],"isStart":false});
            fillet(context, id + "F15", {"entities" : qUnion([Q0]), "radius" : 2 * mm, "tangentPropagation" : true, "allowEdgeOverflow" : false});
        }
        {
            var Q0;
            {var subQ0=sQuery(id+"F0.wireOp",EDGE,"E21.filletArc");var subQ1=sQuery(id+"F0.wireOp",EDGE,"E7");var subQ2=sQuery(id+"F0.wireOp",EDGE,"E6");var subQ3=sQuery(id+"F0.wireOp",EDGE,"E5");var subQ4=sQuery(id+"F0.wireOp",EDGE,"E4");var subQ5=sQuery(id+"F0.wireOp",EDGE,"E22.filletArc");var subQ6=sQuery(id+"F0.wireOp",EDGE,"E1.bottom");var subQ7=sQuery(id+"F0.wireOp",EDGE,"E1.right");var subQ8=sQuery(id+"F0.wireOp",EDGE,"E1.top");var subQ9=sQuery(id+"F0.wireOp",EDGE,"E1.left");var subQ10=sQuery(id+"F0.wireOp",EDGE,"E23.filletArc");var subQ11=sQuery(id+"F0.wireOp",EDGE,"E24.filletArc");Q0=makeQuery(id+"F2.boolean.opBoolean","SPLIT",FACE,{"disambiguationData":[TD([makeQuery(id+"F1.opExtrude","SWEPT_FACE",FACE,{"disambiguationData":[OSD([subQ6])]})])],"derivedFrom":makeQuery(id+"F1.opExtrude","CAP_FACE",FACE,{"disambiguationData":[OSD([subQ6,subQ8,subQ9,subQ7,subQ4,subQ3,subQ2,subQ1,subQ0,subQ5,subQ10,subQ11])],"isStart":true})});}
            var sketch = newSketch(context, id + "F16", { "sketchPlane" : qUnion([Q0])});
            skLineSegment(sketch, "E79", {"start": v(-33, 90) * mm, "end": v(-15, 108) * mm});
            skLineSegment(sketch, "E80", {"start": v(-15, 108) * mm, "end": v(-15, 120) * mm});
            skLineSegment(sketch, "E81", {"start": v(0, 90) * mm, "end": v(0, 120) * mm, "construction": true});
            skCircle(sketch, "E82", {"center": v(0, 120) * mm, "radius": 6 * mm});
            skArc(sketch, "E83", {"start": v(15, 120) * mm, "mid": v(0, 135) * mm, "end": v(-15, 120) * mm});
            skLineSegment(sketch, "E84", {"start": v(15, 120) * mm, "end": v(15, 108) * mm});
            skLineSegment(sketch, "E85", {"start": v(15, 108) * mm, "end": v(33, 90) * mm});
            skLineSegment(sketch, "E86", {"start": v(-15, 108) * mm, "end": v(15, 108) * mm, "construction": true});
            skLineSegment(sketch, "E87", {"start": v(0, 0) * mm, "end": v(80, 0) * mm, "construction": true});
            skLineSegment(sketch, "E88.MirrorCS", {"start": v(15, -120) * mm, "end": v(15, -108) * mm});
            skLineSegment(sketch, "E89.MirrorCS", {"start": v(-33, -90) * mm, "end": v(-15, -108) * mm});
            skLineSegment(sketch, "E90.MirrorCS", {"start": v(-15, -108) * mm, "end": v(-15, -120) * mm});
            skCircle(sketch, "E91.MirrorC", {"center": v(0, -120) * mm, "radius": 6 * mm});
            skLineSegment(sketch, "E92.MirrorCS", {"start": v(-15, -108) * mm, "end": v(15, -108) * mm, "construction": true});
            skLineSegment(sketch, "E93.MirrorCS", {"start": v(0, -90) * mm, "end": v(0, -120) * mm, "construction": true});
            skArc(sketch, "E94.MirrorCS", {"start": v(15, -120) * mm, "mid": v(0, -135) * mm, "end": v(-15, -120) * mm});
            skLineSegment(sketch, "E95.MirrorCS", {"start": v(15, -108) * mm, "end": v(33, -90) * mm});
            skSolve(sketch);
        }
        {
            var Q0;
            Q0=makeQuery(id+"F16.imprint","IMPRINT",FACE,{"disambiguationData":[TD([[makeQuery(id+"F16.imprint","IMPRINT",EDGE,{"derivedFrom":makeQuery(id+"F1.opExtrude","CAP_EDGE",EDGE,{"disambiguationData":[OSD([sQuery(id+"F0.wireOp",EDGE,"E1.left")])],"isStart":true})}),-1.0]])]});
            var Q1;
            {var subQ0=sQuery(id+"F16.wireOp",EDGE,"E79");Q1=makeQuery(id+"F16.imprint","IMPRINT",FACE,{"disambiguationData":[TD([[makeQuery(id+"F16.imprint","IMPRINT",EDGE,{"derivedFrom":subQ0}),-1.0]])]});}
            var Q2;
            {var subQ1=sQuery(id+"F16.wireOp",EDGE,"E89.MirrorCS");Q2=makeQuery(id+"F16.imprint","IMPRINT",FACE,{"disambiguationData":[TD([[makeQuery(id+"F16.imprint","IMPRINT",EDGE,{"derivedFrom":subQ1}),1.0]])]});}
            var Q3;
            Q3=makeQuery(id+"F2.opExtrude","CAP_FACE",FACE,{"disambiguationData":[OSD([sQuery(id+"F0.wireOp",EDGE,"E12"),sQuery(id+"F0.wireOp",EDGE,"E13"),sQuery(id+"F0.wireOp",EDGE,"E14"),sQuery(id+"F0.wireOp",EDGE,"E15"),sQuery(id+"F0.wireOp",EDGE,"E17.filletArc"),sQuery(id+"F0.wireOp",EDGE,"E18.filletArc"),sQuery(id+"F0.wireOp",EDGE,"E19.filletArc"),sQuery(id+"F0.wireOp",EDGE,"E20.filletArc"),sQuery(id+"F0.wireOp",EDGE,"E25.0"),sQuery(id+"F0.wireOp",EDGE,"E25.1"),sQuery(id+"F0.wireOp",EDGE,"E25.2"),sQuery(id+"F0.wireOp",EDGE,"E25.3"),sQuery(id+"F0.wireOp",EDGE,"E25.4"),sQuery(id+"F0.wireOp",EDGE,"E25.5"),sQuery(id+"F0.wireOp",EDGE,"E25.6"),sQuery(id+"F0.wireOp",EDGE,"E25.7")])],"isStart":false});
            extrude(context, id + "F17", {"entities" : qUnion([Q0, Q1, Q2]), "endBound" : BoundingType.UP_TO_SURFACE, "depth" : 25 * mm, "endBoundEntityFace" : qUnion([Q3]), "offsetDistance" : 25 * mm});
        }
    });
